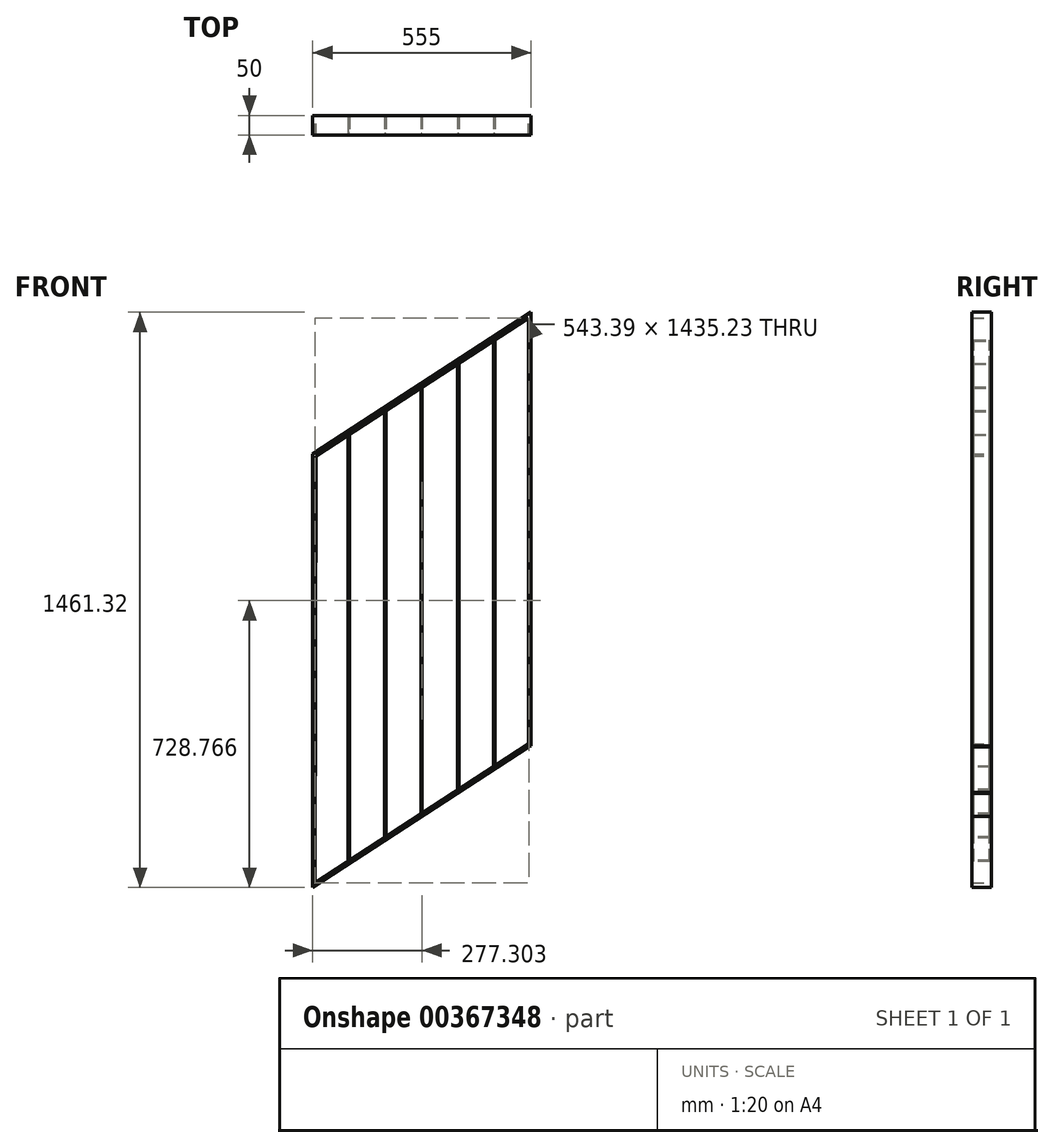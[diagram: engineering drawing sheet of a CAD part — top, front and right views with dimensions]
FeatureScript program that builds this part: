
annotation { "Feature Type Name" : "Feature", "Feature Type Description" : "" }
export const myFeature = defineFeature(function(context is Context, id is Id, definition is map)
    precondition{}
    {
        {
            var Q0;
            Q0=qCreatedBy(makeId("Front.planeOp"),FACE);
            var sketch = newSketch(context, id + "F0", { "sketchPlane" : qUnion([Q0])});
            skLineSegment(sketch, "E0", {"start": v(0, 996.65) * mm, "end": v(555, 996.65) * mm});
            skLineSegment(sketch, "E1", {"start": v(555, 1461.32) * mm, "end": v(0, 1100.62) * mm});
            skLineSegment(sketch, "E2", {"start": v(0, 0) * mm, "end": v(549, 356.5) * mm});
            skLineSegment(sketch, "E3", {"start": v(5.6, 11.15) * mm, "end": v(549, 364.02) * mm});
            skLineSegment(sketch, "E4", {"start": v(0, 1100.62) * mm, "end": v(0, 0) * mm});
            skLineSegment(sketch, "E5", {"start": v(5.6, 11.15) * mm, "end": v(8.15, 1096.34) * mm});
            skLineSegment(sketch, "E6", {"start": v(549, 1446.38) * mm, "end": v(8.15, 1096.34) * mm});
            skLineSegment(sketch, "E7", {"start": v(555, 1461.32) * mm, "end": v(555, 360) * mm});
            skLineSegment(sketch, "E8", {"start": v(555, 360) * mm, "end": v(549, 356.5) * mm});
            skLineSegment(sketch, "E9", {"start": v(549, 364.02) * mm, "end": v(549, 1446.38) * mm});
            skSolve(sketch);
        }
        {
            var Q0;
            Q0 = qSketchRegion(id + "F0", true);
            extrude(context, id + "F1", {"entities" : qUnion([Q0]), "endBound" : BoundingType.SYMMETRIC, "depth" : 50 * mm});
        }
        {
            var Q0;
            Q0=makeQuery(id+"F1.opExtrude","SWEPT_FACE",FACE,{"disambiguationData":[OSD([sQuery(id+"F0.wireOp",EDGE,"E2")])]});
            var sketch = newSketch(context, id + "F2", { "sketchPlane" : qUnion([Q0])});
            skLineSegment(sketch, "E10", {"start": v(0, 0) * mm, "end": v(110, 0) * mm});
            skPoint(sketch, "E10.endSnap0", {"position": v(654.6, 0) * mm});
            skLineSegment(sketch, "E11", {"start": v(110, 0) * mm, "end": v(220, 0) * mm});
            skLineSegment(sketch, "E12", {"start": v(220, 0) * mm, "end": v(330, 0) * mm});
            skLineSegment(sketch, "E13", {"start": v(330, 0) * mm, "end": v(440, 0) * mm});
            skLineSegment(sketch, "E14", {"start": v(440, 0) * mm, "end": v(550, 0) * mm});
            skSolve(sketch);
        }
        {
            var Q0;
            Q0=qCreatedBy(makeId("Front.planeOp"),FACE);
            var sketch = newSketch(context, id + "F3", { "sketchPlane" : qUnion([Q0])});
            skLineSegment(sketch, "E15", {"start": v(90.07, 58.63) * mm, "end": v(90.07, 1150.42) * mm});
            skLineSegment(sketch, "E16", {"start": v(93.62, 61.1) * mm, "end": v(93.62, 1150.42) * mm});
            skLineSegment(sketch, "E17", {"start": v(93.62, 1150.42) * mm, "end": v(90.07, 1150.42) * mm});
            skLineSegment(sketch, "E18", {"start": v(182.55, 118.7) * mm, "end": v(182.55, 1211.45) * mm});
            skLineSegment(sketch, "E19", {"start": v(185.93, 120.78) * mm, "end": v(185.93, 1211.57) * mm});
            skLineSegment(sketch, "E20", {"start": v(185.93, 1211.57) * mm, "end": v(182.55, 1211.45) * mm});
            skLineSegment(sketch, "E21", {"start": v(185.93, 120.78) * mm, "end": v(182.55, 118.7) * mm});
            skLineSegment(sketch, "E22", {"start": v(93.62, 61.1) * mm, "end": v(90.07, 58.63) * mm});
            skLineSegment(sketch, "E23", {"start": v(274.83, 178.49) * mm, "end": v(278.24, 180.66) * mm});
            skLineSegment(sketch, "E24", {"start": v(278.24, 180.66) * mm, "end": v(278.24, 1272.67) * mm});
            skLineSegment(sketch, "E25", {"start": v(274.83, 178.49) * mm, "end": v(274.83, 1269.4) * mm});
            skLineSegment(sketch, "E26", {"start": v(274.83, 1269.4) * mm, "end": v(278.24, 1272.67) * mm});
            skLineSegment(sketch, "E27", {"start": v(368.3, 239.17) * mm, "end": v(371.68, 241.34) * mm});
            skLineSegment(sketch, "E28", {"start": v(371.68, 241.34) * mm, "end": v(371.68, 1333.67) * mm});
            skLineSegment(sketch, "E29", {"start": v(368.3, 239.17) * mm, "end": v(368.3, 1330.59) * mm});
            skLineSegment(sketch, "E30", {"start": v(368.3, 1330.59) * mm, "end": v(371.68, 1333.67) * mm});
            skLineSegment(sketch, "E31", {"start": v(459.42, 298.42) * mm, "end": v(459.42, 1391.96) * mm});
            skLineSegment(sketch, "E32", {"start": v(459.42, 298.42) * mm, "end": v(462.73, 300.6) * mm});
            skLineSegment(sketch, "E33", {"start": v(462.73, 300.6) * mm, "end": v(462.73, 1392.05) * mm});
            skLineSegment(sketch, "E34", {"start": v(462.73, 1392.05) * mm, "end": v(459.42, 1391.96) * mm});
            skSolve(sketch);
        }
        {
            var Q0;
            Q0 = qSketchRegion(id + "F3", true);
            extrude(context, id + "F4", {"entities" : qUnion([Q0]), "operationType" : NewBodyOperationType.ADD, "endBound" : BoundingType.SYMMETRIC, "depth" : 40 * mm});
        }
    });
